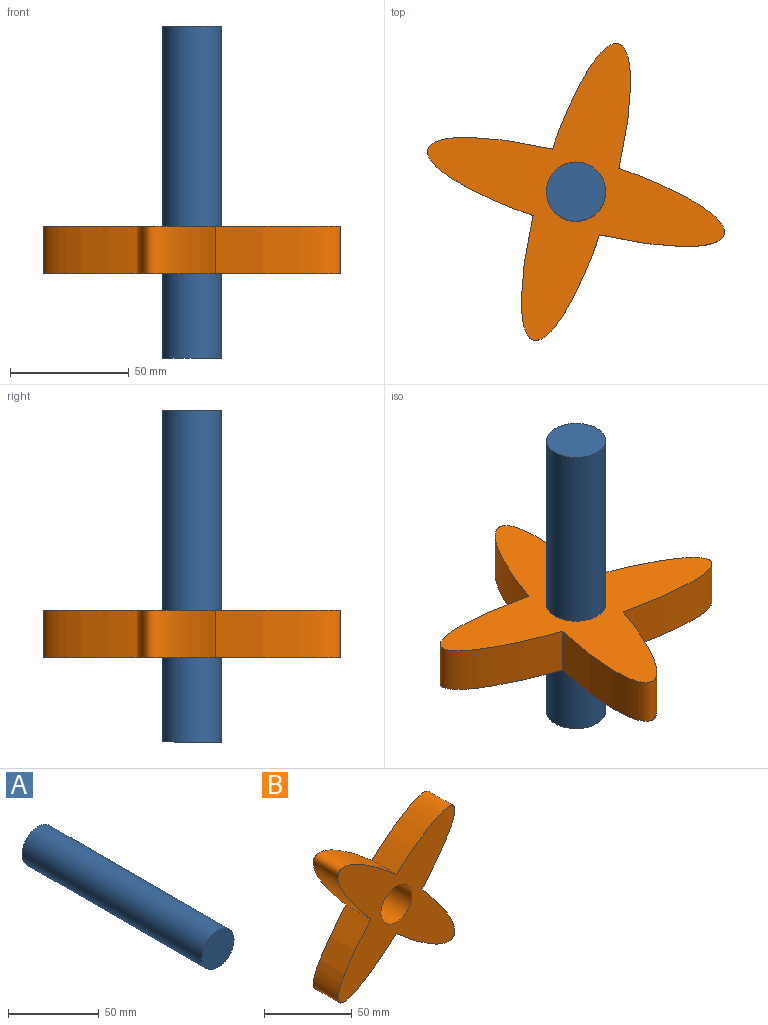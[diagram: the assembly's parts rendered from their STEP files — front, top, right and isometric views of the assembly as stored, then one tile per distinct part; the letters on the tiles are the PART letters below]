
ASSEMBLY  parts=2 mates=1
PART A: 3 faces, bbox 25x140x25 mm
  f0: cylinder r=12.5mm len=140mm, axis (0,1,0), area 10995.6mm2, adj f1,f2
  f1: plane 25x25mm, normal (0,-1,0), area 490.9mm2, adj f0
  f2: plane 25x25mm, normal (0,1,0), area 490.9mm2, adj f0
PART B: 7 faces, bbox 94.3x20x94.3 mm
  f0: extruded ~47.16x47.16mm, area 2180.5mm2, adj f1,f3,f4,f5
  f1: extruded ~47.16x47.16mm, area 2180.5mm2, adj f0,f2,f4,f5
  f2: extruded ~47.16x47.16mm, area 2180.5mm2, adj f1,f3,f4,f5
  f3: extruded ~47.16x47.16mm, area 2180.5mm2, adj f0,f2,f4,f5
  f4: plane 94.34x94.34mm, normal (0,-1,0), area 4750.7mm2, adj f0,f1,f2,f3,f6
  f5: plane 94.34x94.34mm, normal (0,1,0), area 4750.7mm2, adj f0,f1,f2,f3,f6
  f6: cylinder r=12.5mm len=25mm, axis (0,-1,0), area 1570.8mm2, adj f4,f5
PLACE A rot(axis=(-1,0,0),90deg) t=(-1.09,0.48,-45.25)mm fixed
PLACE B rot(axis=(-0.18,0.7,-0.7),159.6deg) t=(-1.09,0.48,-79.76)mm
MATE cylindrical A.f0 <-> B.f6  axis (0,0,-1) through (-1.09,0.48,-45.25)mm
